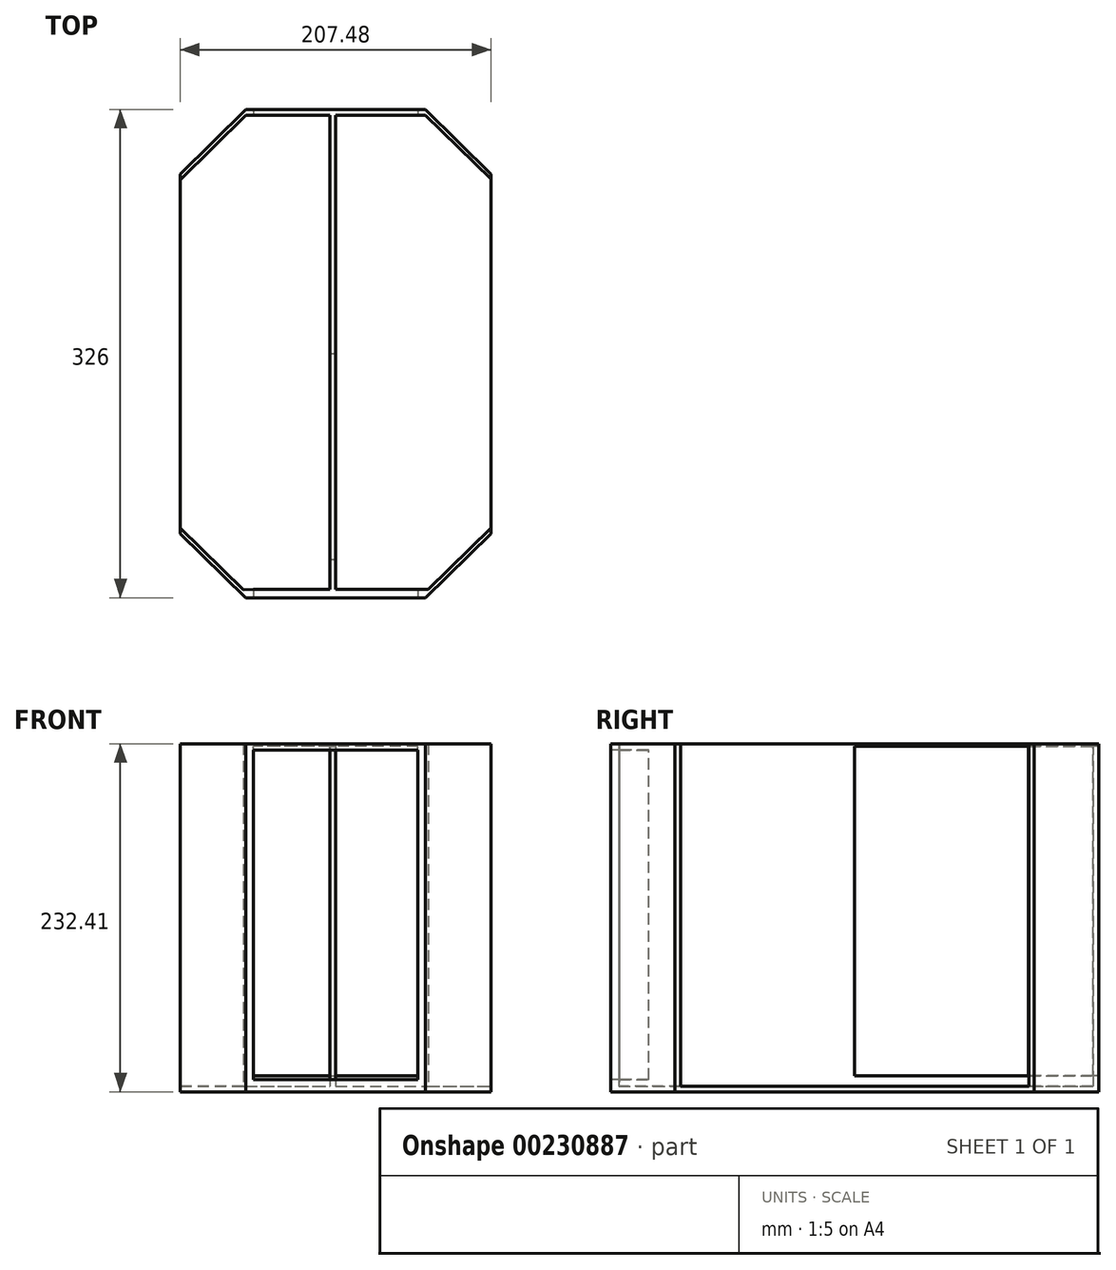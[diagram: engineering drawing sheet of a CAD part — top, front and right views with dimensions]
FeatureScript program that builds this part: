
annotation { "Feature Type Name" : "Feature", "Feature Type Description" : "" }
export const myFeature = defineFeature(function(context is Context, id is Id, definition is map)
    precondition{}
    {
        {
            var Q0;
            Q0=qCreatedBy(makeId("Top.planeOp"),FACE);
            var sketch = newSketch(context, id + "F0", { "sketchPlane" : qUnion([Q0])});
            skLineSegment(sketch, "E0.bottom", {"start": v(103.74, 163) * mm, "end": v(-103.74, 163) * mm});
            skLineSegment(sketch, "E0.top", {"start": v(103.74, -163) * mm, "end": v(-103.74, -163) * mm});
            skLineSegment(sketch, "E0.left", {"start": v(103.74, 163) * mm, "end": v(103.74, -163) * mm});
            skLineSegment(sketch, "E0.right", {"start": v(-103.74, 163) * mm, "end": v(-103.74, -163) * mm});
            skPoint(sketch, "E0.middle", {"position": v(0, 0) * mm});
            skLineSegment(sketch, "E1", {"start": v(60, 163) * mm, "end": v(103.74, 119.82) * mm});
            skLineSegment(sketch, "E2", {"start": v(-60, 163) * mm, "end": v(-103.74, 119.82) * mm});
            skLineSegment(sketch, "E3", {"start": v(-60, -163) * mm, "end": v(-103.74, -120.18) * mm});
            skLineSegment(sketch, "E4", {"start": v(60, -163) * mm, "end": v(103.74, -120.18) * mm});
            skLineSegment(sketch, "E5", {"start": v(-103.74, 116.01) * mm, "end": v(-56.2, 163) * mm});
            skLineSegment(sketch, "E6", {"start": v(-56.19, -163) * mm, "end": v(-103.74, -116.45) * mm});
            skLineSegment(sketch, "E7", {"start": v(56.19, 163) * mm, "end": v(103.74, 116.45) * mm});
            skLineSegment(sketch, "E8", {"start": v(56.1, -163) * mm, "end": v(103.74, -116.37) * mm});
            skLineSegment(sketch, "E9", {"start": v(-60.05, 159.2) * mm, "end": v(60.08, 159.2) * mm});
            skLineSegment(sketch, "E10", {"start": v(-61.7, -157.6) * mm, "end": v(61.95, -157.28) * mm});
            skLineSegment(sketch, "E11", {"start": v(-3.8, -157.45) * mm, "end": v(-3.8, 159.2) * mm});
            skLineSegment(sketch, "E12", {"start": v(0, 159.2) * mm, "end": v(0, -157.44) * mm});
            skSolve(sketch);
        }
        {
            var Q0;
            {var subQ4=sQuery(id+"F0.wireOp",EDGE,"E2");Q0=makeQuery(id+"F0.imprint","IMPRINT",FACE,{"disambiguationData":[TD([[makeQuery(id+"F0.imprint","IMPRINT",EDGE,{"derivedFrom":subQ4}),1.0]])]});}
            var Q1;
            {var subQ5=sQuery(id+"F0.wireOp",EDGE,"E9");Q1=makeQuery(id+"F0.imprint","IMPRINT",FACE,{"disambiguationData":[TD([[makeQuery(id+"F0.imprint","IMPRINT",EDGE,{"derivedFrom":subQ5}),1.0]])]});}
            var Q2;
            {var subQ3=sQuery(id+"F0.wireOp",EDGE,"E9");Q2=makeQuery(id+"F0.imprint","IMPRINT",FACE,{"disambiguationData":[TD([[makeQuery(id+"F0.imprint","IMPRINT",EDGE,{"derivedFrom":subQ3}),-1.0]])]});}
            var Q3;
            {var subQ4=sQuery(id+"F0.wireOp",EDGE,"E1");Q3=makeQuery(id+"F0.imprint","IMPRINT",FACE,{"disambiguationData":[TD([[makeQuery(id+"F0.imprint","IMPRINT",EDGE,{"derivedFrom":subQ4}),-1.0]])]});}
            var Q4;
            {var subQ0=sQuery(id+"F0.wireOp",EDGE,"E4");Q4=makeQuery(id+"F0.imprint","IMPRINT",FACE,{"disambiguationData":[TD([[makeQuery(id+"F0.imprint","IMPRINT",EDGE,{"derivedFrom":subQ0}),1.0]])]});}
            var Q5;
            {var subQ5=sQuery(id+"F0.wireOp",EDGE,"E10");Q5=makeQuery(id+"F0.imprint","IMPRINT",FACE,{"disambiguationData":[TD([[makeQuery(id+"F0.imprint","IMPRINT",EDGE,{"derivedFrom":subQ5}),-1.0]])]});}
            var Q6;
            {var subQ0=sQuery(id+"F0.wireOp",EDGE,"E3");Q6=makeQuery(id+"F0.imprint","IMPRINT",FACE,{"disambiguationData":[TD([[makeQuery(id+"F0.imprint","IMPRINT",EDGE,{"derivedFrom":subQ0}),-1.0]])]});}
            var Q7;
            {var subQ3=sQuery(id+"F0.wireOp",EDGE,"E12");Q7=makeQuery(id+"F0.imprint","IMPRINT",FACE,{"disambiguationData":[TD([[makeQuery(id+"F0.imprint","IMPRINT",EDGE,{"derivedFrom":subQ3}),1.0]])]});}
            var Q8;
            {var subQ9=sQuery(id+"F0.wireOp",EDGE,"E11");Q8=makeQuery(id+"F0.imprint","IMPRINT",FACE,{"disambiguationData":[TD([[makeQuery(id+"F0.imprint","IMPRINT",EDGE,{"derivedFrom":subQ9}),1.0]])]});}
            extrude(context, id + "F1", {"entities" : qUnion([Q0, Q1, Q2, Q3, Q4, Q5, Q6, Q7, Q8]), "oppositeDirection" : true, "depth" : 3.8 * mm});
        }
        {
            var Q0;
            {var subQ5=sQuery(id+"F0.wireOp",EDGE,"E9");Q0=makeQuery(id+"F0.imprint","IMPRINT",FACE,{"disambiguationData":[TD([[makeQuery(id+"F0.imprint","IMPRINT",EDGE,{"derivedFrom":subQ5}),1.0]])]});}
            var Q1;
            {var subQ4=sQuery(id+"F0.wireOp",EDGE,"E1");Q1=makeQuery(id+"F0.imprint","IMPRINT",FACE,{"disambiguationData":[TD([[makeQuery(id+"F0.imprint","IMPRINT",EDGE,{"derivedFrom":subQ4}),-1.0]])]});}
            var Q2;
            {var subQ4=sQuery(id+"F0.wireOp",EDGE,"E2");Q2=makeQuery(id+"F0.imprint","IMPRINT",FACE,{"disambiguationData":[TD([[makeQuery(id+"F0.imprint","IMPRINT",EDGE,{"derivedFrom":subQ4}),1.0]])]});}
            var Q3;
            {var subQ5=sQuery(id+"F0.wireOp",EDGE,"E10");Q3=makeQuery(id+"F0.imprint","IMPRINT",FACE,{"disambiguationData":[TD([[makeQuery(id+"F0.imprint","IMPRINT",EDGE,{"derivedFrom":subQ5}),-1.0]])]});}
            var Q4;
            {var subQ0=sQuery(id+"F0.wireOp",EDGE,"E3");Q4=makeQuery(id+"F0.imprint","IMPRINT",FACE,{"disambiguationData":[TD([[makeQuery(id+"F0.imprint","IMPRINT",EDGE,{"derivedFrom":subQ0}),-1.0]])]});}
            var Q5;
            {var subQ0=sQuery(id+"F0.wireOp",EDGE,"E4");Q5=makeQuery(id+"F0.imprint","IMPRINT",FACE,{"disambiguationData":[TD([[makeQuery(id+"F0.imprint","IMPRINT",EDGE,{"derivedFrom":subQ0}),1.0]])]});}
            var Q6;
            {var subQ0=sQuery(id+"F0.wireOp",EDGE,"E11");Q6=makeQuery(id+"F0.imprint","IMPRINT",FACE,{"disambiguationData":[TD([[makeQuery(id+"F0.imprint","IMPRINT",EDGE,{"derivedFrom":subQ0}),-1.0]])]});}
            extrude(context, id + "F2", {"entities" : qUnion([Q0, Q1, Q2, Q3, Q4, Q5, Q6]), "operationType" : NewBodyOperationType.ADD, "depth" : 228.6 * mm});
        }
        {
            var Q0;
            {var subQ0=sQuery(id+"F0.wireOp",EDGE,"E0.top");Q0=makeQuery(id+"F2.boolean.opBoolean","MERGE",FACE,{"derivedFrom":[makeQuery(id+"F1.opExtrude","SWEPT_FACE",FACE,{"disambiguationData":[OSD([subQ0])]}),makeQuery(id+"F2.opExtrude","SWEPT_FACE",FACE,{"disambiguationData":[OSD([subQ0])]})]});}
            var sketch = newSketch(context, id + "F3", { "sketchPlane" : qUnion([Q0])});
            skLineSegment(sketch, "E13", {"start": v(0, 0) * mm, "end": v(0, 228.6) * mm});
            skLineSegment(sketch, "E14.bottom", {"start": v(55, 4.3) * mm, "end": v(-55, 4.3) * mm});
            skLineSegment(sketch, "E14.top", {"start": v(55, 224.3) * mm, "end": v(-55, 224.3) * mm});
            skLineSegment(sketch, "E14.left", {"start": v(55, 4.3) * mm, "end": v(55, 224.3) * mm});
            skLineSegment(sketch, "E14.right", {"start": v(-55, 4.3) * mm, "end": v(-55, 224.3) * mm});
            skPoint(sketch, "E14.middle", {"position": v(0, 114.3) * mm});
            skSolve(sketch);
        }
        {
            var Q0;
            {var subQ5=sQuery(id+"F3.wireOp",EDGE,"E14.left");Q0=makeQuery(id+"F3.imprint","IMPRINT",FACE,{"disambiguationData":[TD([[makeQuery(id+"F3.imprint","IMPRINT",EDGE,{"derivedFrom":subQ5}),1.0]])]});}
            var Q1;
            {var subQ5=sQuery(id+"F3.wireOp",EDGE,"E14.right");Q1=makeQuery(id+"F3.imprint","IMPRINT",FACE,{"disambiguationData":[TD([[makeQuery(id+"F3.imprint","IMPRINT",EDGE,{"derivedFrom":subQ5}),-1.0]])]});}
            extrude(context, id + "F4", {"entities" : qUnion([Q0, Q1]), "operationType" : NewBodyOperationType.REMOVE, "oppositeDirection" : true, "depth" : 25.4 * mm});
        }
        {
            var Q0;
            Q0=qCreatedBy(makeId("Front.planeOp"),FACE);
            var sketch = newSketch(context, id + "F5", { "sketchPlane" : qUnion([Q0])});
            skLineSegment(sketch, "E15", {"start": v(0, 233.68) * mm, "end": v(0, 0) * mm});
            skLineSegment(sketch, "E16.bottom", {"start": v(-55, 226.84) * mm, "end": v(55, 226.84) * mm});
            skLineSegment(sketch, "E16.top", {"start": v(-55, 6.84) * mm, "end": v(55, 6.84) * mm});
            skLineSegment(sketch, "E16.left", {"start": v(-55, 226.84) * mm, "end": v(-55, 6.84) * mm});
            skLineSegment(sketch, "E16.right", {"start": v(55, 226.84) * mm, "end": v(55, 6.84) * mm});
            skPoint(sketch, "E16.middle", {"position": v(0, 116.84) * mm});
            skSolve(sketch);
        }
        {
            var Q0;
            {var subQ5=sQuery(id+"F5.wireOp",EDGE,"E16.right");Q0=makeQuery(id+"F5.imprint","IMPRINT",FACE,{"disambiguationData":[TD([[makeQuery(id+"F5.imprint","IMPRINT",EDGE,{"derivedFrom":subQ5}),-1.0]])]});}
            var sketch = newSketch(context, id + "F6", { "sketchPlane" : qUnion([Q0])});
            skSolve(sketch);
        }
        {
            var Q0;
            Q0 = qSketchRegion(id + "F6", true);
            var Q1;
            {var subQ5=sQuery(id+"F5.wireOp",EDGE,"E16.right");Q1=makeQuery(id+"F5.imprint","IMPRINT",FACE,{"disambiguationData":[TD([[makeQuery(id+"F5.imprint","IMPRINT",EDGE,{"derivedFrom":subQ5}),-1.0]])]});}
            var Q2;
            {var subQ5=sQuery(id+"F5.wireOp",EDGE,"E16.left");Q2=makeQuery(id+"F5.imprint","IMPRINT",FACE,{"disambiguationData":[TD([[makeQuery(id+"F5.imprint","IMPRINT",EDGE,{"derivedFrom":subQ5}),1.0]])]});}
            extrude(context, id + "F7", {"entities" : qUnion([Q0, Q1, Q2]), "operationType" : NewBodyOperationType.REMOVE, "oppositeDirection" : true, "depth" : 228.6 * mm});
        }
    });
